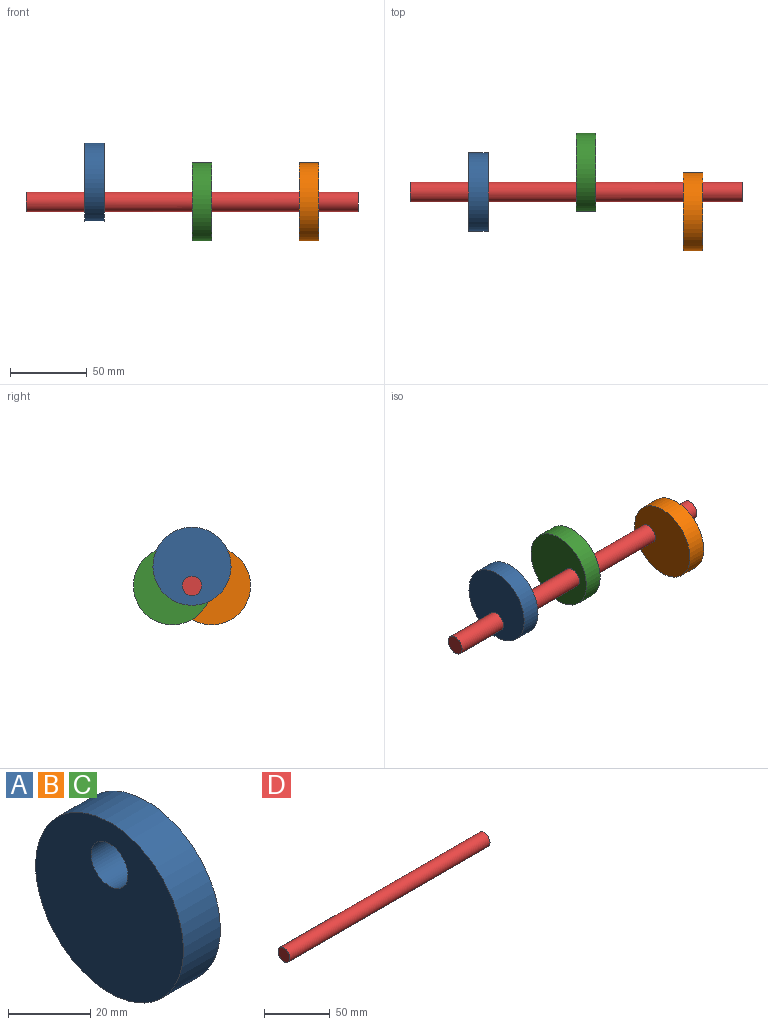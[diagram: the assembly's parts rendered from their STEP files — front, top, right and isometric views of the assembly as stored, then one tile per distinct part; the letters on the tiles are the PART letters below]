
ASSEMBLY  parts=4 mates=3
PART A: 4 faces, bbox 12.7x50.8x50.8 mm
  f0: plane 50.8x50.8mm, normal (1,0,0), area 1900.2mm2, adj f2,f3
  f1: plane 50.8x50.8mm, normal (-1,0,0), area 1900.2mm2, adj f2,f3
  f2: cylinder r=25.4mm len=50.8mm, axis (1,0,0), area 2026.8mm2, adj f0,f1
  f3: cylinder r=6.35mm len=12.7mm, axis (-1,0,0), area 506.7mm2, adj f0,f1
PART B: same geometry as A
PART C: same geometry as A
PART D: 3 faces, bbox 215.9x12.7x12.7 mm
  f0: plane 12.7x12.7mm, normal (1,0,0), area 126.7mm2, adj f1
  f1: cylinder r=6.35mm len=215.9mm, axis (-1,0,0), area 8614mm2, adj f0,f2
  f2: plane 12.7x12.7mm, normal (-1,0,0), area 126.7mm2, adj f1
PLACE A rot(axis=(0,-1,0),180deg) t=(76.2,0,57.15)mm
PLACE B rot(axis=(-1,0,0),90deg) t=(152.4,-57.15,0)mm
PLACE C rot(axis=(1,0,0),90deg) t=(82.55,57.15,0)mm
PLACE D t=(12.7,0,-57.15)mm
MATE fastened D.f1 <-> A.f3  axis (-1,0,0) through (44.45,0,0)mm
MATE fastened D.f1 <-> C.f3  axis (-1,0,0) through (114.3,0,0)mm
MATE fastened D.f1 <-> B.f3  axis (-1,0,0) through (184.15,0,0)mm
